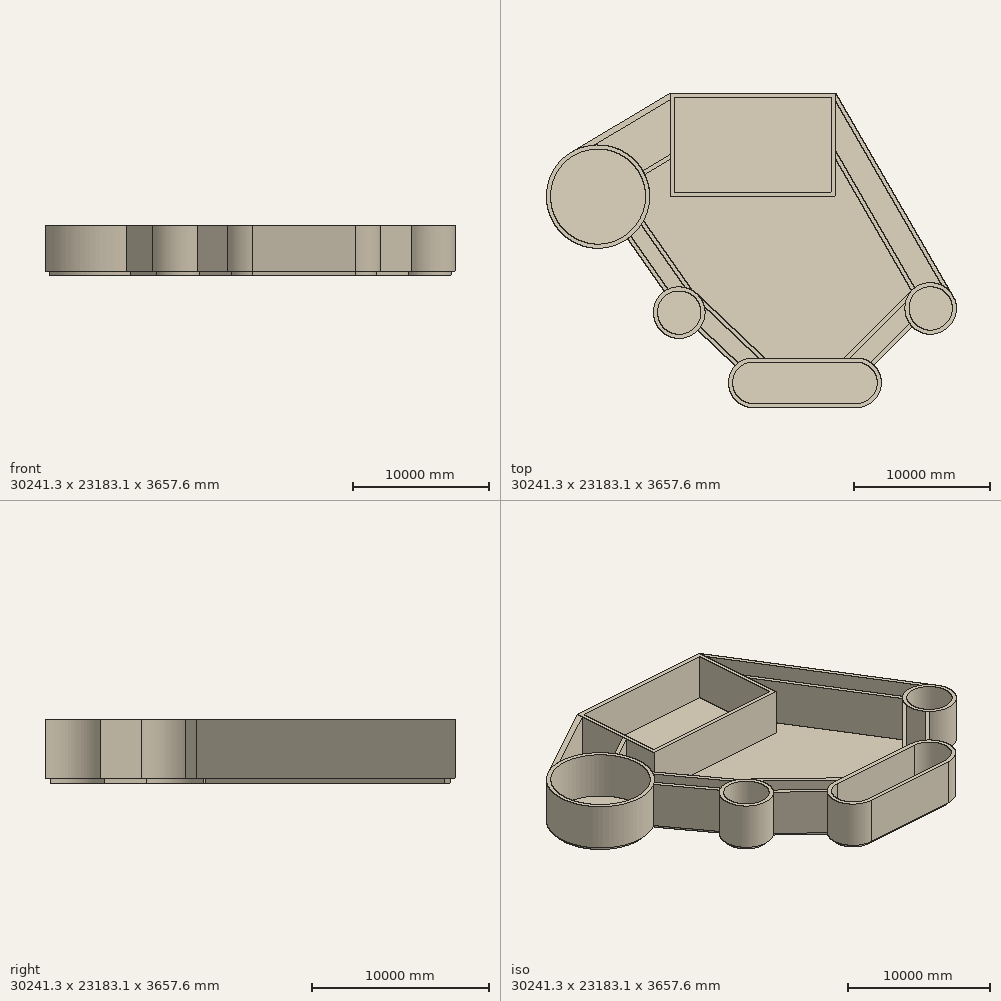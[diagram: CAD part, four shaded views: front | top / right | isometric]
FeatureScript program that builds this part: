
annotation { "Feature Type Name" : "Feature", "Feature Type Description" : "" }
export const myFeature = defineFeature(function(context is Context, id is Id, definition is map)
    precondition{}
    {
        {
            var Q0;
            Q0=qCreatedBy(makeId("Top.planeOp"),FACE);
            var sketch = newSketch(context, id + "F0", { "sketchPlane" : qUnion([Q0])});
            skLineSegment(sketch, "E0", {"start": v(-6112.03, 4876.8) * mm, "end": v(6079.97, 4876.8) * mm});
            skLineSegment(sketch, "E1", {"start": v(-6112.03, 4876.8) * mm, "end": v(-6112.03, -2743.2) * mm});
            skLineSegment(sketch, "E2", {"start": v(-6112.03, -2743.2) * mm, "end": v(6079.97, -2743.2) * mm});
            skLineSegment(sketch, "E3", {"start": v(6079.97, -2743.2) * mm, "end": v(6079.97, 4876.8) * mm});
            skLineSegment(sketch, "E4", {"start": v(6079.97, 4876.8) * mm, "end": v(14878.79, -10363.2) * mm});
            skCircle(sketch, "E5", {"center": v(13080.25, -10991.13) * mm, "radius": 1905 * mm});
            skPoint(sketch, "E5.second.point", {"position": v(11972.96, -12541.26) * mm});
            skPoint(sketch, "E5.third.point", {"position": v(12265.25, -9269.27) * mm});
            skLineSegment(sketch, "E6", {"start": v(6079.97, 0) * mm, "end": v(11679.98, -9699.5) * mm});
            skCircle(sketch, "E7", {"center": v(-11446.03, -2743.2) * mm, "radius": 3810 * mm});
            skLineSegment(sketch, "E8", {"start": v(-6112.03, 4876.8) * mm, "end": v(-13398.47, 528.5) * mm});
            skLineSegment(sketch, "E9", {"start": v(-7996.85, -1124.8) * mm, "end": v(-6112.03, 0) * mm});
            skCircle(sketch, "E10", {"center": v(-5460.25, -11300.88) * mm, "radius": 1905 * mm});
            skLineSegment(sketch, "E11", {"start": v(-9262.27, -5865.26) * mm, "end": v(-6552.13, -9739.85) * mm});
            skLineSegment(sketch, "E12", {"start": v(-4514.36, -9647.3) * mm, "end": v(-8086.5, -4540.33) * mm});
            skLineSegment(sketch, "E13.bottom", {"start": v(-5807.23, 4572) * mm, "end": v(5775.17, 4572) * mm});
            skLineSegment(sketch, "E13.top", {"start": v(-5807.23, -2438.4) * mm, "end": v(5775.17, -2438.4) * mm});
            skLineSegment(sketch, "E13.left", {"start": v(-5807.23, 4572) * mm, "end": v(-5807.23, -2438.4) * mm});
            skLineSegment(sketch, "E13.right", {"start": v(5775.17, 4572) * mm, "end": v(5775.17, -2438.4) * mm});
            skLineSegment(sketch, "E14", {"start": v(-5807.23, 4572) * mm, "end": v(-11694.5, 1058.69) * mm});
            skCircle(sketch, "E15", {"center": v(-11446.03, -2743.2) * mm, "radius": 3505.2 * mm});
            skLineSegment(sketch, "E16", {"start": v(-9019.5, -5680.55) * mm, "end": v(-6288.3, -9585.26) * mm});
            skLineSegment(sketch, "E17", {"start": v(-8257.14, -4828.16) * mm, "end": v(-5027.32, -9445.73) * mm});
            skCircle(sketch, "E18", {"center": v(-5460.25, -11300.88) * mm, "radius": 1600.2 * mm});
            skCircle(sketch, "E19", {"center": v(13080.25, -10991.13) * mm, "radius": 1600.2 * mm});
            skLineSegment(sketch, "E20", {"start": v(-8137.52, -853.8) * mm, "end": v(-6112.03, 354.95) * mm});
            skLineSegment(sketch, "E21", {"start": v(6079.97, 609.6) * mm, "end": v(11909.86, -9488.06) * mm});
            skLineSegment(sketch, "E22", {"start": v(6079.97, 4267.2) * mm, "end": v(13895.25, -9269.27) * mm});
            skLineSegment(sketch, "E23.bottom", {"start": v(0, -14648.73) * mm, "end": v(7620, -14648.73) * mm});
            skLineSegment(sketch, "E23.top", {"start": v(0, -18306.33) * mm, "end": v(7620, -18306.33) * mm});
            skArc(sketch, "E24", {"start": v(0, -14648.73) * mm, "mid": v(-1828.8, -16477.53) * mm, "end": v(0, -18306.33) * mm});
            skArc(sketch, "E25", {"start": v(7620, -18306.33) * mm, "mid": v(9448.8, -16477.53) * mm, "end": v(7620, -14648.73) * mm});
            skLineSegment(sketch, "E26", {"start": v(-1327.16, -15219.3) * mm, "end": v(-4298.98, -12401.84) * mm});
            skLineSegment(sketch, "E27", {"start": v(8910.06, -15181.28) * mm, "end": v(11951.44, -12125.34) * mm});
            skLineSegment(sketch, "E28", {"start": v(11730, -9647.3) * mm, "end": v(6752.42, -14648.73) * mm});
            skLineSegment(sketch, "E29", {"start": v(839.87, -14648.73) * mm, "end": v(-4149.6, -9918.42) * mm});
            skLineSegment(sketch, "E30", {"start": v(7182.45, -14648.73) * mm, "end": v(11216.9, -10594.95) * mm});
            skLineSegment(sketch, "E31", {"start": v(8675.98, -14984.4) * mm, "end": v(11537.7, -12108.97) * mm});
            skLineSegment(sketch, "E32", {"start": v(-3609.2, -10850.76) * mm, "end": v(396.85, -14648.73) * mm});
            skLineSegment(sketch, "E33", {"start": v(-3885.9, -12373.46) * mm, "end": v(-1098.9, -15015.7) * mm});
            skArc(sketch, "E34", {"start": v(0, -14953.53) * mm, "mid": v(-1524, -16477.53) * mm, "end": v(0, -18001.53) * mm});
            skArc(sketch, "E35", {"start": v(7620, -18001.53) * mm, "mid": v(9144, -16477.53) * mm, "end": v(7620, -14953.53) * mm});
            skLineSegment(sketch, "E36", {"start": v(0, -14953.53) * mm, "end": v(7620, -14953.53) * mm});
            skLineSegment(sketch, "E37", {"start": v(0, -18001.53) * mm, "end": v(7620, -18001.53) * mm});
            skSolve(sketch);
        }
        {
            var Q0;
            {var subQ1=sQuery(id+"F0.wireOp",EDGE,"E0");Q0=makeQuery(id+"F0.imprint","IMPRINT",FACE,{"disambiguationData":[TD([[makeQuery(id+"F0.imprint","IMPRINT",EDGE,{"derivedFrom":subQ1}),-1.0]])]});}
            var Q1;
            Q1=makeQuery(id+"F0.imprint","IMPRINT",FACE,{"disambiguationData":[TD([[makeQuery(id+"F0.imprint","IMPRINT",EDGE,{"derivedFrom":sQuery(id+"F0.wireOp",EDGE,"E15")}),-1.0]])]});
            var Q2;
            Q2=makeQuery(id+"F0.imprint","IMPRINT",FACE,{"disambiguationData":[TD([[makeQuery(id+"F0.imprint","IMPRINT",EDGE,{"derivedFrom":sQuery(id+"F0.wireOp",EDGE,"E18")}),-1.0]])]});
            var Q3;
            {var subQ1=sQuery(id+"F0.wireOp",EDGE,"E23.top");Q3=makeQuery(id+"F0.imprint","IMPRINT",FACE,{"disambiguationData":[TD([[makeQuery(id+"F0.imprint","IMPRINT",EDGE,{"derivedFrom":subQ1}),1.0]])]});}
            var Q4;
            Q4=makeQuery(id+"F0.imprint","IMPRINT",FACE,{"disambiguationData":[TD([[makeQuery(id+"F0.imprint","IMPRINT",EDGE,{"derivedFrom":sQuery(id+"F0.wireOp",EDGE,"E19")}),-1.0]])]});
            extrude(context, id + "F1", {"entities" : qUnion([Q0, Q1, Q2, Q3, Q4]), "depth" : 3352.8 * mm, "offsetDistance" : 25.4 * mm});
        }
        {
            var Q0;
            {var subQ0=sQuery(id+"F0.wireOp",EDGE,"E21");Q0=makeQuery(id+"F0.imprint","IMPRINT",FACE,{"disambiguationData":[TD([[makeQuery(id+"F0.imprint","IMPRINT",EDGE,{"derivedFrom":subQ0}),-1.0]])]});}
            var Q1;
            {var subQ3=sQuery(id+"F0.wireOp",EDGE,"E22");Q1=makeQuery(id+"F0.imprint","IMPRINT",FACE,{"disambiguationData":[TD([[makeQuery(id+"F0.imprint","IMPRINT",EDGE,{"derivedFrom":subQ3}),1.0]])]});}
            var Q2;
            {var subQ5=sQuery(id+"F0.wireOp",EDGE,"E30");Q2=makeQuery(id+"F0.imprint","IMPRINT",FACE,{"disambiguationData":[TD([[makeQuery(id+"F0.imprint","IMPRINT",EDGE,{"derivedFrom":subQ5}),1.0]])]});}
            var Q3;
            {var subQ0=sQuery(id+"F0.wireOp",EDGE,"E31");Q3=makeQuery(id+"F0.imprint","IMPRINT",FACE,{"disambiguationData":[TD([[makeQuery(id+"F0.imprint","IMPRINT",EDGE,{"derivedFrom":subQ0}),-1.0]])]});}
            var Q4;
            {var subQ0=sQuery(id+"F0.wireOp",EDGE,"E29");Q4=makeQuery(id+"F0.imprint","IMPRINT",FACE,{"disambiguationData":[TD([[makeQuery(id+"F0.imprint","IMPRINT",EDGE,{"derivedFrom":subQ0}),1.0]])]});}
            var Q5;
            {var subQ0=sQuery(id+"F0.wireOp",EDGE,"E33");Q5=makeQuery(id+"F0.imprint","IMPRINT",FACE,{"disambiguationData":[TD([[makeQuery(id+"F0.imprint","IMPRINT",EDGE,{"derivedFrom":subQ0}),-1.0]])]});}
            var Q6;
            {var subQ0=sQuery(id+"F0.wireOp",EDGE,"E12");Q6=makeQuery(id+"F0.imprint","IMPRINT",FACE,{"disambiguationData":[TD([[makeQuery(id+"F0.imprint","IMPRINT",EDGE,{"derivedFrom":subQ0}),1.0]])]});}
            var Q7;
            {var subQ0=sQuery(id+"F0.wireOp",EDGE,"E11");Q7=makeQuery(id+"F0.imprint","IMPRINT",FACE,{"disambiguationData":[TD([[makeQuery(id+"F0.imprint","IMPRINT",EDGE,{"derivedFrom":subQ0}),1.0]])]});}
            var Q8;
            {var subQ0=sQuery(id+"F0.wireOp",EDGE,"E9");Q8=makeQuery(id+"F0.imprint","IMPRINT",FACE,{"disambiguationData":[TD([[makeQuery(id+"F0.imprint","IMPRINT",EDGE,{"derivedFrom":subQ0}),1.0]])]});}
            var Q9;
            {var subQ0=sQuery(id+"F0.wireOp",EDGE,"E8");Q9=makeQuery(id+"F0.imprint","IMPRINT",FACE,{"disambiguationData":[TD([[makeQuery(id+"F0.imprint","IMPRINT",EDGE,{"derivedFrom":subQ0}),1.0]])]});}
            extrude(context, id + "F2", {"entities" : qUnion([Q0, Q1, Q2, Q3, Q4, Q5, Q6, Q7, Q8, Q9]), "depth" : 3352.8 * mm, "offsetDistance" : 25.4 * mm});
        }
        {
            var Q0;
            Q0=makeQuery(id+"F0.imprint","IMPRINT",FACE,{"disambiguationData":[TD([[makeQuery(id+"F0.imprint","IMPRINT",EDGE,{"derivedFrom":sQuery(id+"F0.wireOp",EDGE,"E15")}),1.0]])]});
            var Q1;
            {var subQ8=sQuery(id+"F0.wireOp",EDGE,"E2");Q1=makeQuery(id+"F0.imprint","IMPRINT",FACE,{"disambiguationData":[TD([[makeQuery(id+"F0.imprint","IMPRINT",EDGE,{"derivedFrom":subQ8}),-1.0]])]});}
            var Q2;
            {var subQ0=sQuery(id+"F0.wireOp",EDGE,"E16");Q2=makeQuery(id+"F0.imprint","IMPRINT",FACE,{"disambiguationData":[TD([[makeQuery(id+"F0.imprint","IMPRINT",EDGE,{"derivedFrom":subQ0}),1.0]])]});}
            var Q3;
            Q3=makeQuery(id+"F0.imprint","IMPRINT",FACE,{"disambiguationData":[TD([[makeQuery(id+"F0.imprint","IMPRINT",EDGE,{"derivedFrom":sQuery(id+"F0.wireOp",EDGE,"E18")}),1.0]])]});
            var Q4;
            Q4=makeQuery(id+"F0.imprint","IMPRINT",FACE,{"disambiguationData":[TD([[makeQuery(id+"F0.imprint","IMPRINT",EDGE,{"derivedFrom":sQuery(id+"F0.wireOp",EDGE,"E13.bottom")}),-1.0]])]});
            var Q5;
            {var subQ0=sQuery(id+"F0.wireOp",EDGE,"E20");Q5=makeQuery(id+"F0.imprint","IMPRINT",FACE,{"disambiguationData":[TD([[makeQuery(id+"F0.imprint","IMPRINT",EDGE,{"derivedFrom":subQ0}),1.0]])]});}
            var Q6;
            {var subQ0=sQuery(id+"F0.wireOp",EDGE,"E21");Q6=makeQuery(id+"F0.imprint","IMPRINT",FACE,{"disambiguationData":[TD([[makeQuery(id+"F0.imprint","IMPRINT",EDGE,{"derivedFrom":subQ0}),1.0]])]});}
            var Q7;
            Q7=makeQuery(id+"F0.imprint","IMPRINT",FACE,{"disambiguationData":[TD([[makeQuery(id+"F0.imprint","IMPRINT",EDGE,{"derivedFrom":sQuery(id+"F0.wireOp",EDGE,"E19")}),1.0]])]});
            var Q8;
            {var subQ4=sQuery(id+"F0.wireOp",EDGE,"E30");Q8=makeQuery(id+"F0.imprint","IMPRINT",FACE,{"disambiguationData":[TD([[makeQuery(id+"F0.imprint","IMPRINT",EDGE,{"derivedFrom":subQ4}),-1.0]])]});}
            var Q9;
            {var subQ4=sQuery(id+"F0.wireOp",EDGE,"E32");Q9=makeQuery(id+"F0.imprint","IMPRINT",FACE,{"disambiguationData":[TD([[makeQuery(id+"F0.imprint","IMPRINT",EDGE,{"derivedFrom":subQ4}),-1.0]])]});}
            var Q10;
            Q10=makeQuery(id+"F0.imprint","IMPRINT",FACE,{"disambiguationData":[TD([[makeQuery(id+"F0.imprint","IMPRINT",EDGE,{"derivedFrom":sQuery(id+"F0.wireOp",EDGE,"E34")}),1.0]])]});
            extrude(context, id + "F3", {"entities" : qUnion([Q0, Q1, Q2, Q3, Q4, Q5, Q6, Q7, Q8, Q9, Q10]), "oppositeDirection" : true, "depth" : 304.8 * mm, "offsetDistance" : 25.4 * mm});
        }
    });
